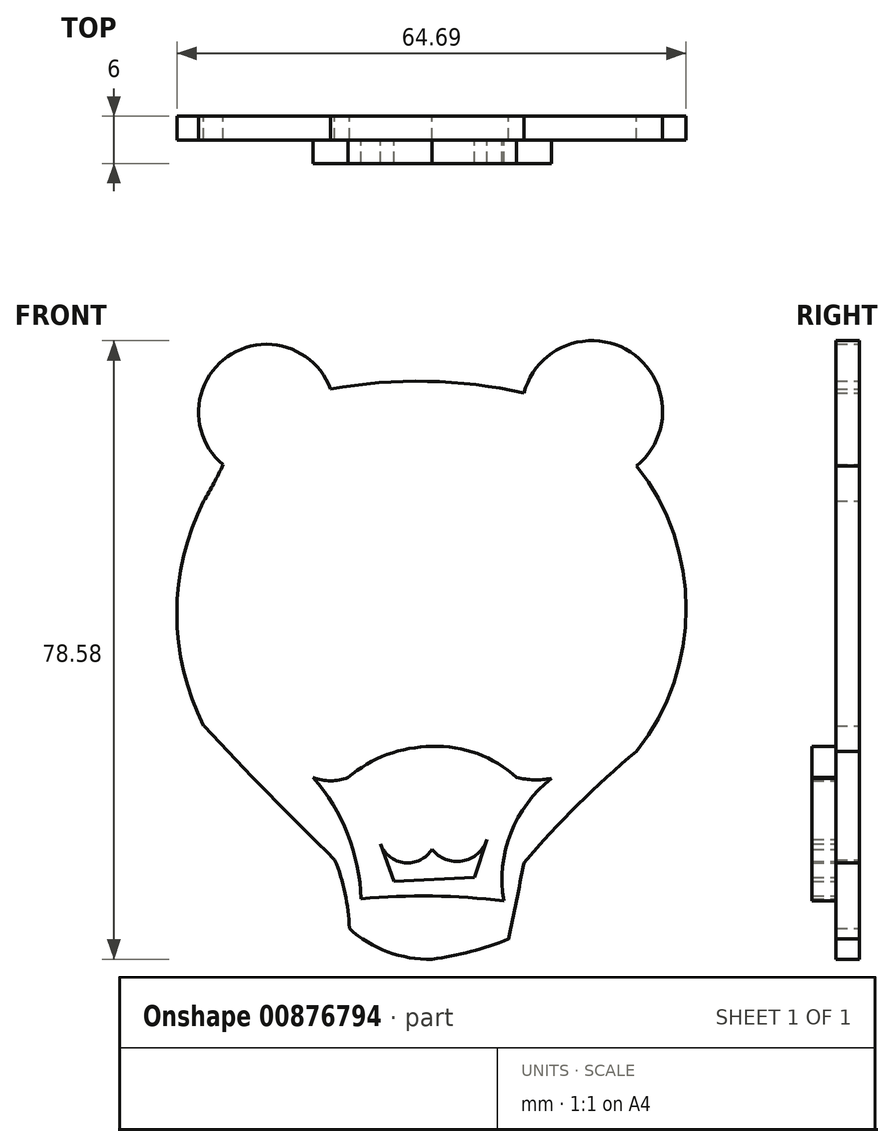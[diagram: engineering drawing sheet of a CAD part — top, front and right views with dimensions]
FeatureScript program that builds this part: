
annotation { "Feature Type Name" : "Feature", "Feature Type Description" : "" }
export const myFeature = defineFeature(function(context is Context, id is Id, definition is map)
    precondition{}
    {
        {
            var Q0;
            Q0=qCreatedBy(makeId("Front.planeOp"),FACE);
            var sketch = newSketch(context, id + "F0", { "sketchPlane" : qUnion([Q0])});
            skPoint(sketch, "E0", {"position": v(10.61, -21.47) * mm});
            skPoint(sketch, "E1", {"position": v(8.16, -26.11) * mm});
            skPoint(sketch, "E2", {"position": v(8.16, -54.65) * mm});
            skPoint(sketch, "E3", {"position": v(26.65, -80.38) * mm});
            skPoint(sketch, "E4", {"position": v(24.8, -71.65) * mm});
            skPoint(sketch, "E5", {"position": v(48.83, -12.37) * mm});
            skPoint(sketch, "E6", {"position": v(63.14, -21.61) * mm});
            skPoint(sketch, "E7", {"position": v(63.14, -57.87) * mm});
            skPoint(sketch, "E8", {"position": v(48.83, -72.03) * mm});
            skPoint(sketch, "E9", {"position": v(46.86, -81.74) * mm});
            skPoint(sketch, "E10", {"position": v(37.15, -84.28) * mm});
            skArc(sketch, "E11", {"start": v(8.16, -26.11) * mm, "mid": v(4.74, -40.38) * mm, "end": v(8.16, -54.65) * mm});
            skArc(sketch, "E12", {"start": v(26.65, -80.38) * mm, "mid": v(26.1, -75.93) * mm, "end": v(24.8, -71.65) * mm});
            skArc(sketch, "E13", {"start": v(46.86, -81.74) * mm, "mid": v(47.86, -76.89) * mm, "end": v(48.83, -72.03) * mm});
            skArc(sketch, "E14", {"start": v(63.14, -57.87) * mm, "mid": v(69.43, -39.74) * mm, "end": v(63.14, -21.61) * mm});
            skArc(sketch, "E15", {"start": v(8.16, -26.11) * mm, "mid": v(9.43, -23.82) * mm, "end": v(10.61, -21.47) * mm});
            skPoint(sketch, "E16", {"position": v(24.26, -11.87) * mm});
            skArc(sketch, "E17", {"start": v(24.26, -11.87) * mm, "mid": v(11.15, -7.75) * mm, "end": v(10.61, -21.47) * mm});
            skArc(sketch, "E18", {"start": v(63.14, -21.61) * mm, "mid": v(62.35, -7.15) * mm, "end": v(48.83, -12.37) * mm});
            skArc(sketch, "E19", {"start": v(48.83, -12.37) * mm, "mid": v(36.57, -10.88) * mm, "end": v(24.26, -11.87) * mm});
            skArc(sketch, "E20", {"start": v(8.16, -54.65) * mm, "mid": v(16.38, -63.25) * mm, "end": v(24.8, -71.65) * mm});
            skArc(sketch, "E21", {"start": v(63.14, -57.87) * mm, "mid": v(55.69, -64.65) * mm, "end": v(48.83, -72.03) * mm});
            skArc(sketch, "E22", {"start": v(26.65, -80.38) * mm, "mid": v(31.52, -83.36) * mm, "end": v(37.15, -84.28) * mm});
            skArc(sketch, "E23", {"start": v(37.15, -84.28) * mm, "mid": v(42.08, -83.31) * mm, "end": v(46.86, -81.74) * mm});
            skSolve(sketch);
        }
        {
            var Q0;
            Q0 = qSketchRegion(id + "F0", true);
            extrude(context, id + "F1", {"entities" : qUnion([Q0]), "depth" : 3 * mm, "offsetDistance" : 25.4 * mm});
        }
        {
            var Q0;
            Q0=makeQuery(id+"F1.opExtrude","CAP_FACE",FACE,{"disambiguationData":[OSD([sQuery(id+"F0.wireOp",EDGE,"E11"),sQuery(id+"F0.wireOp",EDGE,"E12"),sQuery(id+"F0.wireOp",EDGE,"E13"),sQuery(id+"F0.wireOp",EDGE,"E14"),sQuery(id+"F0.wireOp",EDGE,"E15"),sQuery(id+"F0.wireOp",EDGE,"E17"),sQuery(id+"F0.wireOp",EDGE,"E18"),sQuery(id+"F0.wireOp",EDGE,"E19"),sQuery(id+"F0.wireOp",EDGE,"E20"),sQuery(id+"F0.wireOp",EDGE,"E21"),sQuery(id+"F0.wireOp",EDGE,"E22"),sQuery(id+"F0.wireOp",EDGE,"E23")])],"isStart":false});
            var sketch = newSketch(context, id + "F2", { "sketchPlane" : qUnion([Q0])});
            skPoint(sketch, "E24", {"position": v(22.07, -61.21) * mm});
            skPoint(sketch, "E25", {"position": v(28.14, -76.63) * mm});
            skPoint(sketch, "E26", {"position": v(46.26, -76.89) * mm});
            skPoint(sketch, "E26.positionSnap0", {"position": v(47.86, -76.89) * mm});
            skPoint(sketch, "E27", {"position": v(52.34, -61.32) * mm});
            skPoint(sketch, "E28", {"position": v(42.56, -73.93) * mm});
            skPoint(sketch, "E29", {"position": v(44.13, -69.1) * mm});
            skPoint(sketch, "E30", {"position": v(30.62, -69.65) * mm});
            skPoint(sketch, "E31", {"position": v(32.3, -74.38) * mm});
            skPoint(sketch, "E32", {"position": v(37.15, -70.33) * mm});
            skPoint(sketch, "E33", {"position": v(37.15, -57.27) * mm});
            skArc(sketch, "E34", {"start": v(28.14, -76.63) * mm, "mid": v(26.43, -68.4) * mm, "end": v(22.07, -61.21) * mm});
            skPoint(sketch, "E35", {"position": v(26.48, -61.21) * mm});
            skPoint(sketch, "E36", {"position": v(47.9, -61.21) * mm});
            skArc(sketch, "E37", {"start": v(22.07, -61.21) * mm, "mid": v(24.27, -61.62) * mm, "end": v(26.48, -61.21) * mm});
            skArc(sketch, "E38", {"start": v(37.15, -57.27) * mm, "mid": v(31.46, -58.3) * mm, "end": v(26.48, -61.21) * mm});
            skArc(sketch, "E39", {"start": v(47.9, -61.21) * mm, "mid": v(42.92, -58.18) * mm, "end": v(37.15, -57.27) * mm});
            skArc(sketch, "E40", {"start": v(47.9, -61.21) * mm, "mid": v(50.11, -61.5) * mm, "end": v(52.34, -61.32) * mm});
            skArc(sketch, "E41", {"start": v(52.34, -61.32) * mm, "mid": v(47.15, -68.27) * mm, "end": v(46.26, -76.89) * mm});
            skArc(sketch, "E42", {"start": v(46.26, -76.89) * mm, "mid": v(37.2, -76.27) * mm, "end": v(28.14, -76.63) * mm});
            skPoint(sketch, "E43", {"position": v(30.18, -58.83) * mm});
            skPoint(sketch, "E44", {"position": v(30.27, -66.89) * mm});
            skPoint(sketch, "E45", {"position": v(43.91, -66.78) * mm});
            skPoint(sketch, "E46", {"position": v(44.03, -58.64) * mm});
            skArc(sketch, "E47", {"start": v(30.18, -58.83) * mm, "mid": v(29.68, -62.86) * mm, "end": v(30.27, -66.89) * mm});
            skArc(sketch, "E48", {"start": v(26.48, -61.21) * mm, "mid": v(27.65, -64.53) * mm, "end": v(30.27, -66.89) * mm});
            skArc(sketch, "E49", {"start": v(43.91, -66.78) * mm, "mid": v(44.72, -62.72) * mm, "end": v(44.03, -58.64) * mm});
            skArc(sketch, "E50", {"start": v(43.91, -66.78) * mm, "mid": v(46.56, -64.46) * mm, "end": v(47.9, -61.21) * mm});
            skLineSegment(sketch, "E51", {"start": v(30.62, -69.65) * mm, "end": v(32.3, -74.38) * mm});
            skLineSegment(sketch, "E52", {"start": v(44.13, -69.1) * mm, "end": v(42.56, -73.93) * mm});
            skArc(sketch, "E53", {"start": v(30.62, -69.65) * mm, "mid": v(33.67, -72.05) * mm, "end": v(37.15, -70.33) * mm});
            skArc(sketch, "E54", {"start": v(37.15, -70.33) * mm, "mid": v(41, -71.8) * mm, "end": v(44.13, -69.1) * mm});
            skLineSegment(sketch, "E55", {"start": v(32.3, -74.38) * mm, "end": v(42.56, -73.93) * mm});
            skPoint(sketch, "E56", {"position": v(46.07, -36.27) * mm});
            skPoint(sketch, "E57", {"position": v(45.8, -38.02) * mm});
            skPoint(sketch, "E58", {"position": v(52.77, -41.77) * mm});
            skPoint(sketch, "E59", {"position": v(55.59, -57.06) * mm});
            skPoint(sketch, "E60", {"position": v(56.4, -48.07) * mm});
            skPoint(sketch, "E61", {"position": v(47.14, -48.07) * mm});
            skPoint(sketch, "E62", {"position": v(42.85, -39.5) * mm});
            skPoint(sketch, "E63", {"position": v(42.85, -34.93) * mm});
            skPoint(sketch, "E64", {"position": v(51.8, -42.9) * mm});
            skPoint(sketch, "E65", {"position": v(52.67, -44.8) * mm});
            skPoint(sketch, "E66", {"position": v(53.7, -46.4) * mm});
            skPoint(sketch, "E67", {"position": v(54.66, -49.43) * mm});
            skPoint(sketch, "E68", {"position": v(54.66, -51.83) * mm});
            skPoint(sketch, "E69", {"position": v(55.46, -53.34) * mm});
            skPoint(sketch, "E70", {"position": v(45.5, -56.13) * mm});
            skPoint(sketch, "E71", {"position": v(44.14, -53.34) * mm});
            skSolve(sketch);
        }
        {
            var Q0;
            Q0 = qSketchRegion(id + "F2", true);
            extrude(context, id + "F3", {"entities" : qUnion([Q0]), "operationType" : NewBodyOperationType.ADD, "depth" : 3 * mm, "offsetDistance" : 25.4 * mm});
        }
        {
            var Q0;
            Q0 = qSketchRegion(id + "F2", true);
            extrude(context, id + "F4", {"entities" : qUnion([Q0]), "operationType" : NewBodyOperationType.ADD, "depth" : 3 * mm, "offsetDistance" : 25.4 * mm});
        }
    });
